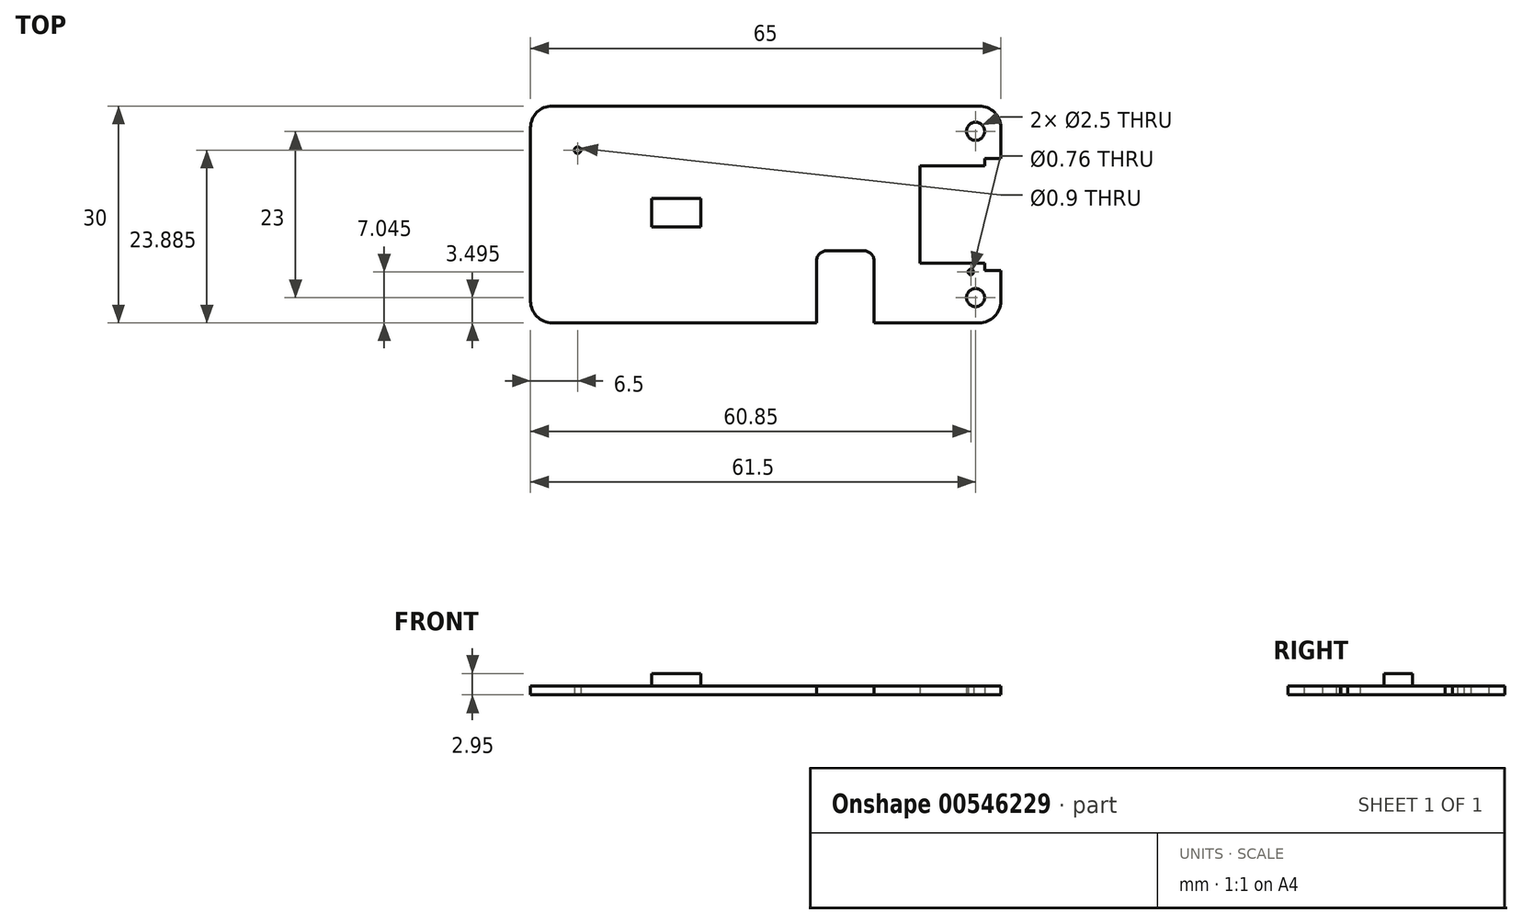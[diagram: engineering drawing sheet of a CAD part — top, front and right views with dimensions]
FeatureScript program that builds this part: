
annotation { "Feature Type Name" : "Feature", "Feature Type Description" : "" }
export const myFeature = defineFeature(function(context is Context, id is Id, definition is map)
    precondition{}
    {
        {
            var Q0;
            Q0=qCreatedBy(makeId("Top.planeOp"),FACE);
            var sketch = newSketch(context, id + "F0", { "sketchPlane" : qUnion([Q0])});
            skLineSegment(sketch, "E0.bottom", {"start": v(-28.75, 11.22) * mm, "end": v(30.25, 11.22) * mm});
            skLineSegment(sketch, "E0.top", {"start": v(-28.75, -18.78) * mm, "end": v(7.75, -18.78) * mm});
            skLineSegment(sketch, "E0.left", {"start": v(-31.75, 8.22) * mm, "end": v(-31.75, -15.78) * mm});
            skLineSegment(sketch, "E0.right", {"start": v(33.25, 8.22) * mm, "end": v(33.25, 3.97) * mm});
            skPoint(sketch, "E1.visualSharp", {"position": v(-31.75, 11.22) * mm});
            skArc(sketch, "E1.filletArc", {"start": v(-28.75, 11.22) * mm, "mid": v(-30.87, 10.34) * mm, "end": v(-31.75, 8.22) * mm});
            skPoint(sketch, "E2.visualSharp", {"position": v(33.25, 11.22) * mm});
            skArc(sketch, "E2.filletArc", {"start": v(33.25, 8.22) * mm, "mid": v(32.37, 10.34) * mm, "end": v(30.25, 11.22) * mm});
            skPoint(sketch, "E3.visualSharp", {"position": v(33.25, -18.78) * mm});
            skArc(sketch, "E3.filletArc", {"start": v(30.25, -18.78) * mm, "mid": v(32.37, -17.9) * mm, "end": v(33.25, -15.78) * mm});
            skPoint(sketch, "E4.visualSharp", {"position": v(-31.75, -18.78) * mm});
            skArc(sketch, "E4.filletArc", {"start": v(-31.75, -15.78) * mm, "mid": v(-30.87, -17.9) * mm, "end": v(-28.75, -18.78) * mm});
            skCircle(sketch, "E5", {"center": v(29.75, 7.72) * mm, "radius": 1.25 * mm});
            skCircle(sketch, "E6", {"center": v(29.75, -15.28) * mm, "radius": 1.25 * mm});
            skLineSegment(sketch, "E7.bottom", {"start": v(22.05, 2.97) * mm, "end": v(31.05, 2.97) * mm});
            skLineSegment(sketch, "E7.top", {"start": v(22.05, -10.53) * mm, "end": v(31.05, -10.53) * mm});
            skLineSegment(sketch, "E7.left", {"start": v(22.05, 2.97) * mm, "end": v(22.05, -10.53) * mm});
            skLineSegment(sketch, "E8.bottom", {"start": v(31.05, 3.97) * mm, "end": v(33.25, 3.97) * mm});
            skLineSegment(sketch, "E8.top", {"start": v(31.05, -11.53) * mm, "end": v(33.25, -11.53) * mm});
            skLineSegment(sketch, "E8.left", {"start": v(31.05, 3.97) * mm, "end": v(31.05, 2.97) * mm});
            skLineSegment(sketch, "E9.trimOffspring", {"start": v(33.25, -11.53) * mm, "end": v(33.25, -15.78) * mm});
            skLineSegment(sketch, "E10.trimOffspring", {"start": v(31.05, -10.53) * mm, "end": v(31.05, -11.53) * mm});
            skLineSegment(sketch, "E11.bottom", {"start": v(9.25, -8.8) * mm, "end": v(14.25, -8.8) * mm});
            skLineSegment(sketch, "E11.left", {"start": v(7.75, -10.3) * mm, "end": v(7.75, -18.78) * mm});
            skLineSegment(sketch, "E11.right", {"start": v(15.75, -10.3) * mm, "end": v(15.75, -18.78) * mm});
            skPoint(sketch, "E12.visualSharp", {"position": v(7.75, -8.8) * mm});
            skArc(sketch, "E12.filletArc", {"start": v(9.25, -8.8) * mm, "mid": v(8.19, -9.24) * mm, "end": v(7.75, -10.3) * mm});
            skPoint(sketch, "E13.visualSharp", {"position": v(15.75, -8.8) * mm});
            skArc(sketch, "E13.filletArc", {"start": v(15.75, -10.3) * mm, "mid": v(15.31, -9.24) * mm, "end": v(14.25, -8.8) * mm});
            skLineSegment(sketch, "E14.trimOffspring", {"start": v(15.75, -18.78) * mm, "end": v(30.25, -18.78) * mm});
            skCircle(sketch, "E15", {"center": v(29.1, -11.73) * mm, "radius": 0.38 * mm});
            skCircle(sketch, "E16", {"center": v(-25.25, 5.1) * mm, "radius": 0.45 * mm});
            skLineSegment(sketch, "E17.bottom", {"start": v(-15.05, -1.58) * mm, "end": v(-8.2, -1.58) * mm});
            skLineSegment(sketch, "E17.top", {"start": v(-15.05, -5.48) * mm, "end": v(-8.2, -5.48) * mm});
            skLineSegment(sketch, "E17.left", {"start": v(-15.05, -1.58) * mm, "end": v(-15.05, -5.48) * mm});
            skLineSegment(sketch, "E17.right", {"start": v(-8.2, -1.58) * mm, "end": v(-8.2, -5.48) * mm});
            skSolve(sketch);
        }
        {
            var Q0;
            Q0=makeQuery(id+"F0.imprint","IMPRINT",FACE,{"disambiguationData":[TD([[makeQuery(id+"F0.imprint","IMPRINT",EDGE,{"derivedFrom":sQuery(id+"F0.wireOp",EDGE,"E0.bottom")}),-1.0]])]});
            var Q1;
            Q1=makeQuery(id+"F0.imprint","IMPRINT",FACE,{"disambiguationData":[TD([[makeQuery(id+"F0.imprint","IMPRINT",EDGE,{"derivedFrom":sQuery(id+"F0.wireOp",EDGE,"E17.bottom")}),-1.0]])]});
            extrude(context, id + "F1", {"entities" : qUnion([Q0, Q1]), "depth" : 1.2 * mm, "offsetDistance" : 25 * mm});
        }
        {
            var Q0;
            Q0=makeQuery(id+"F0.imprint","IMPRINT",FACE,{"disambiguationData":[TD([[makeQuery(id+"F0.imprint","IMPRINT",EDGE,{"derivedFrom":sQuery(id+"F0.wireOp",EDGE,"E17.bottom")}),-1.0]])]});
            extrude(context, id + "F2", {"entities" : qUnion([Q0]), "operationType" : NewBodyOperationType.ADD, "depth" : 2.95 * mm, "offsetDistance" : 25 * mm, "hasSecondDirection" : true, "secondDirectionOppositeDirection" : false, "secondDirectionDepth" : 1.2 * mm});
        }
    });
